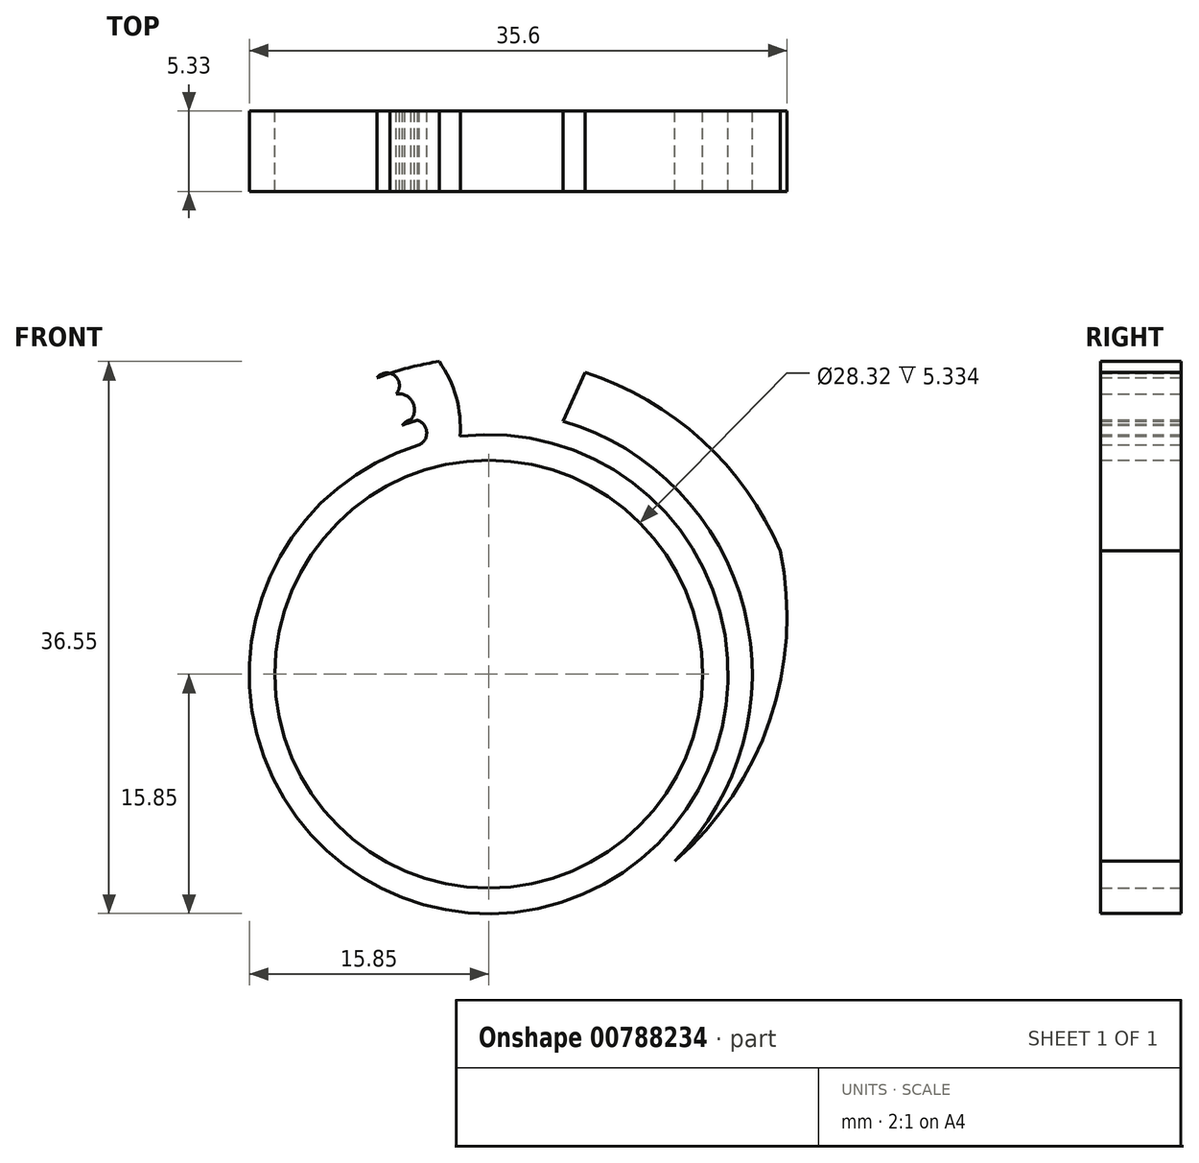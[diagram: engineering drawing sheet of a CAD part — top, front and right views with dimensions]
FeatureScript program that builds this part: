
annotation { "Feature Type Name" : "Feature", "Feature Type Description" : "" }
export const myFeature = defineFeature(function(context is Context, id is Id, definition is map)
    precondition{}
    {
        {
            var Q0;
            Q0=qCreatedBy(makeId("Front.planeOp"),FACE);
            var sketch = newSketch(context, id + "F0", { "sketchPlane" : qUnion([Q0])});
            skArc(sketch, "E0", {"start": v(-1.95, 17.34) * mm, "mid": v(-17.43, -0.98) * mm, "end": v(0, -17.45) * mm});
            skArc(sketch, "E1", {"start": v(19.3, 8.16) * mm, "mid": v(14.13, 15.48) * mm, "end": v(6.37, 19.97) * mm});
            skArc(sketch, "E2.MirrorCS", {"start": v(19.3, 8.16) * mm, "mid": v(15.46, -9.02) * mm, "end": v(0, -17.45) * mm});
            skArc(sketch, "E3", {"start": v(19.46, 0.3) * mm, "mid": v(15.58, 11.67) * mm, "end": v(5.75, 18.6) * mm});
            skPoint(sketch, "E4.endSnap0", {"position": v(0, 19.46) * mm});
            skArc(sketch, "E5.trimOffspring", {"start": v(-3.28, 20.7) * mm, "mid": v(-10.4, 18.2) * mm, "end": v(-16.18, 13.33) * mm});
            skArc(sketch, "E6.trimOffspring", {"start": v(-2.5, 19.3) * mm, "mid": v(-11.4, 15.78) * mm, "end": v(-17.54, 8.43) * mm});
            skPoint(sketch, "E7.orphan", {"position": v(0, 5.94) * mm});
            skCircle(sketch, "E8.converted", {"center": v(0, 0) * mm, "radius": 14.16 * mm});
            skCircle(sketch, "E9.converted", {"center": v(0, 0) * mm, "radius": 15.85 * mm});
            skLineSegment(sketch, "E10", {"start": v(6.37, 19.97) * mm, "end": v(4.91, 16.75) * mm});
            skPoint(sketch, "E11.orphan", {"position": v(-19.3, 8.16) * mm});
            skArc(sketch, "E12.trimOffspring", {"start": v(0, -17.45) * mm, "mid": v(17.28, -2.48) * mm, "end": v(4.91, 16.75) * mm});
            skPoint(sketch, "E13.orphan", {"position": v(0, -18.14) * mm});
            skLineSegment(sketch, "E14", {"start": v(-4.02, 21.71) * mm, "end": v(-3.87, 21.43) * mm});
            skLineSegment(sketch, "E15", {"start": v(3.48, 21.43) * mm, "end": v(-3.87, 21.43) * mm});
            skArc(sketch, "E16", {"start": v(-16.18, 13.33) * mm, "mid": v(-17.41, 11.03) * mm, "end": v(-17.54, 8.43) * mm});
            skArc(sketch, "E17", {"start": v(-17.54, 8.43) * mm, "mid": v(-18.33, 2.42) * mm, "end": v(-17.1, -3.52) * mm});
            skArc(sketch, "E18", {"start": v(-5.7, 16.5) * mm, "mid": v(-5.04, 18) * mm, "end": v(-6.68, 18.28) * mm});
            skArc(sketch, "E19", {"start": v(-6.68, 18.28) * mm, "mid": v(-6.01, 19.5) * mm, "end": v(-7.4, 19.61) * mm});
            skArc(sketch, "E20", {"start": v(-4.85, 15.1) * mm, "mid": v(-4.24, 16.43) * mm, "end": v(-5.7, 16.5) * mm});
            skArc(sketch, "E21", {"start": v(-2.24, 13.98) * mm, "mid": v(-2.05, 17.92) * mm, "end": v(-3.87, 21.43) * mm});
            skPoint(sketch, "E22.start.orphan", {"position": v(0, 14.16) * mm});
            skSolve(sketch);
        }
        {
            var Q0;
            {var subQ0=sQuery(id+"F0.wireOp",EDGE,"E12.trimOffspring");var subQ1=sQuery(id+"F0.wireOp",EDGE,"E2.MirrorCS");var subQ2=makeQuery(id+"F0.imprint","INTERSECT",VERTEX,{"disambiguationData":[OD(0.0)],"derivedFrom":[subQ1,subQ0]});Q0=makeQuery(id+"F0.imprint","IMPRINT",FACE,{"disambiguationData":[TD([[makeQuery(id+"F0.imprint","IMPRINT",EDGE,{"disambiguationData":[TD([[subQ2,1.0]])],"derivedFrom":subQ1}),1.0]])]});}
            var Q1;
            {var subQ0=sQuery(id+"F0.wireOp",EDGE,"E18");var subQ1=sQuery(id+"F0.wireOp",EDGE,"E0");var subQ3=makeQuery(id+"F0.imprint","INTERSECT",VERTEX,{"derivedFrom":[subQ1,subQ0]});Q1=makeQuery(id+"F0.imprint","IMPRINT",FACE,{"disambiguationData":[TD([[makeQuery(id+"F0.imprint","IMPRINT",EDGE,{"disambiguationData":[TD([[subQ3,-1.0]])],"derivedFrom":subQ1}),1.0]])]});}
            var Q2;
            {var subQ0=sQuery(id+"F0.wireOp",EDGE,"E1");Q2=makeQuery(id+"F0.imprint","IMPRINT",FACE,{"disambiguationData":[TD([[makeQuery(id+"F0.imprint","IMPRINT",EDGE,{"derivedFrom":subQ0}),1.0]])]});}
            var Q3;
            {var subQ0=sQuery(id+"F0.wireOp",EDGE,"E3");Q3=makeQuery(id+"F0.imprint","IMPRINT",FACE,{"disambiguationData":[TD([[makeQuery(id+"F0.imprint","IMPRINT",EDGE,{"derivedFrom":subQ0}),1.0]])]});}
            var Q4;
            {var subQ0=sQuery(id+"F0.wireOp",EDGE,"E19");var subQ1=sQuery(id+"F0.wireOp",EDGE,"E5.trimOffspring");var subQ2=makeQuery(id+"F0.imprint","INTERSECT",VERTEX,{"disambiguationData":[OD(0.0)],"derivedFrom":[subQ1,subQ0]});Q4=makeQuery(id+"F0.imprint","IMPRINT",FACE,{"disambiguationData":[TD([[makeQuery(id+"F0.imprint","IMPRINT",EDGE,{"disambiguationData":[TD([[subQ2,1.0]])],"derivedFrom":subQ1}),-1.0]])]});}
            var Q5;
            {var subQ0=sQuery(id+"F0.wireOp",EDGE,"E20");var subQ1=sQuery(id+"F0.wireOp",EDGE,"E9.converted");var subQ2=makeQuery(id+"F0.imprint","INTERSECT",VERTEX,{"disambiguationData":[OD(0.0)],"derivedFrom":[subQ1,subQ0]});Q5=makeQuery(id+"F0.imprint","IMPRINT",FACE,{"disambiguationData":[TD([[makeQuery(id+"F0.imprint","IMPRINT",EDGE,{"disambiguationData":[TD([[subQ2,1.0]])],"derivedFrom":subQ1}),1.0]])]});}
            var Q6;
            {var subQ0=sQuery(id+"F0.wireOp",EDGE,"E21");var subQ1=sQuery(id+"F0.wireOp",EDGE,"E0");var subQ2=makeQuery(id+"F0.imprint","INTERSECT",VERTEX,{"derivedFrom":[subQ1,subQ0]});Q6=makeQuery(id+"F0.imprint","IMPRINT",FACE,{"disambiguationData":[TD([[makeQuery(id+"F0.imprint","IMPRINT",EDGE,{"disambiguationData":[TD([[subQ2,-1.0]])],"derivedFrom":subQ1}),1.0]])]});}
            var Q7;
            {var subQ0=sQuery(id+"F0.wireOp",EDGE,"E20");var subQ1=sQuery(id+"F0.wireOp",EDGE,"E0");var subQ2=makeQuery(id+"F0.imprint","INTERSECT",VERTEX,{"derivedFrom":[subQ1,subQ0]});Q7=makeQuery(id+"F0.imprint","IMPRINT",FACE,{"disambiguationData":[TD([[makeQuery(id+"F0.imprint","IMPRINT",EDGE,{"disambiguationData":[TD([[subQ2,-1.0]])],"derivedFrom":subQ1}),-1.0]])]});}
            var Q8;
            {var subQ1=sQuery(id+"F0.wireOp",EDGE,"E18");var subQ2=sQuery(id+"F0.wireOp",EDGE,"E0");var subQ4=makeQuery(id+"F0.imprint","INTERSECT",VERTEX,{"derivedFrom":[subQ2,subQ1]});Q8=makeQuery(id+"F0.imprint","IMPRINT",FACE,{"disambiguationData":[TD([[makeQuery(id+"F0.imprint","IMPRINT",EDGE,{"disambiguationData":[TD([[subQ4,-1.0]])],"derivedFrom":subQ1}),1.0]])]});}
            var Q9;
            {var subQ1=sQuery(id+"F0.wireOp",EDGE,"E5.trimOffspring");var subQ5=sQuery(id+"F0.wireOp",EDGE,"E21");var subQ9=makeQuery(id+"F0.imprint","INTERSECT",VERTEX,{"derivedFrom":[subQ1,subQ5]});Q9=makeQuery(id+"F0.imprint","IMPRINT",FACE,{"disambiguationData":[TD([[makeQuery(id+"F0.imprint","IMPRINT",EDGE,{"disambiguationData":[TD([[subQ9,-1.0]])],"derivedFrom":subQ1}),1.0]])]});}
            var Q10;
            {var subQ5=sQuery(id+"F0.wireOp",EDGE,"E0");var subQ7=sQuery(id+"F0.wireOp",EDGE,"E21");var subQ9=makeQuery(id+"F0.imprint","INTERSECT",VERTEX,{"derivedFrom":[subQ5,subQ7]});Q10=makeQuery(id+"F0.imprint","IMPRINT",FACE,{"disambiguationData":[TD([[makeQuery(id+"F0.imprint","IMPRINT",EDGE,{"disambiguationData":[TD([[subQ9,-1.0]])],"derivedFrom":subQ5}),-1.0]])]});}
            var Q11;
            Q11=makeQuery(id+"F0.imprint","IMPRINT",FACE,{"disambiguationData":[TD([[makeQuery(id+"F0.imprint","IMPRINT",EDGE,{"derivedFrom":sQuery(id+"F0.wireOp",EDGE,"E8.converted")}),-1.0]])]});
            extrude(context, id + "F1", {"entities" : qUnion([Q0, Q1, Q2, Q3, Q4, Q5, Q6, Q7, Q8, Q9, Q10, Q11]), "depth" : 5.33 * mm, "offsetDistance" : 25.4 * mm});
        }
    });
